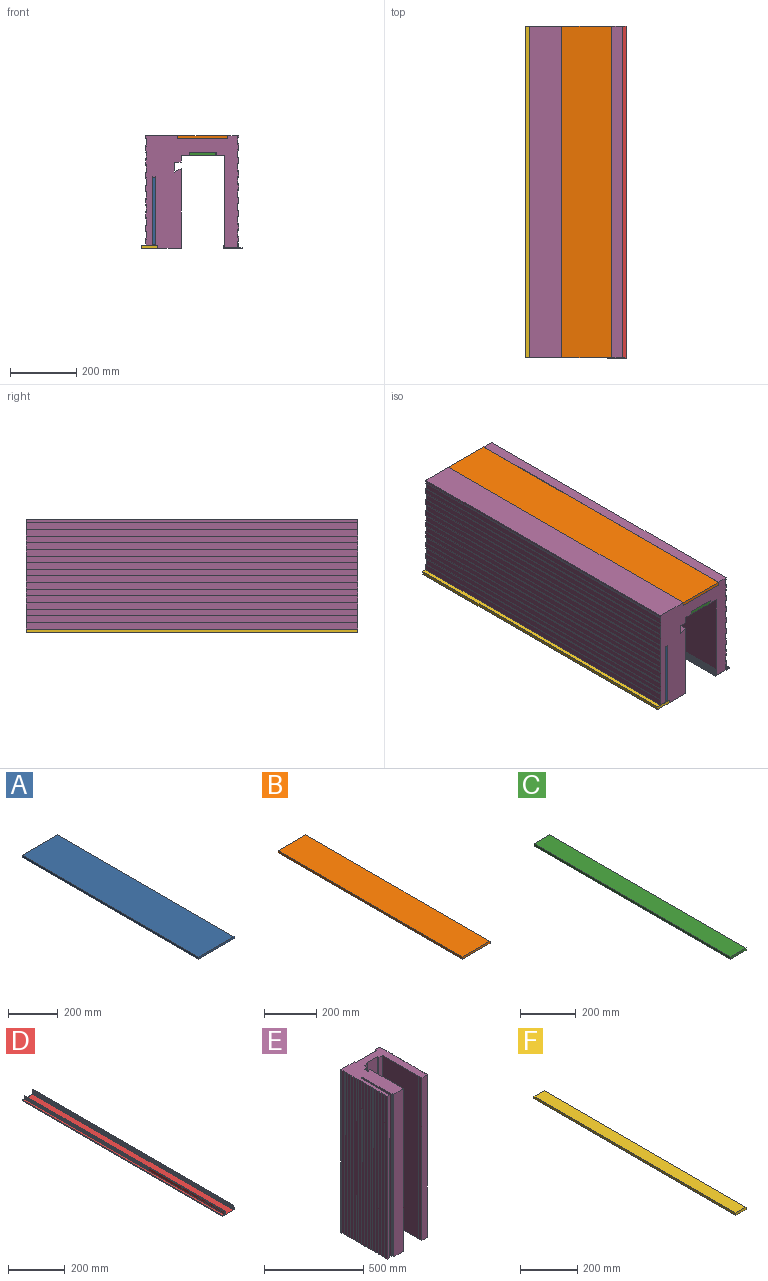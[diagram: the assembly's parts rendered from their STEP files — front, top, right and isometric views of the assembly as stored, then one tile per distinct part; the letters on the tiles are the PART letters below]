
ASSEMBLY  parts=6 mates=5
PART A: 6 faces, bbox 200x1000x10 mm
  f0: plane 1000x10mm, normal (-1,0,0), area 10000mm2, adj f1,f3,f4,f5
  f1: plane 1000x200mm, normal (0,0,-1), area 200000mm2, adj f0,f2,f4,f5
  f2: plane 1000x10mm, normal (1,0,0), area 10000mm2, adj f1,f3,f4,f5
  f3: plane 1000x200mm, normal (0,0,1), area 200000mm2, adj f0,f2,f4,f5
  f4: plane 200x10mm, normal (0,-1,0), area 2000mm2, adj f0,f1,f2,f3
  f5: plane 200x10mm, normal (0,1,0), area 2000mm2, adj f0,f1,f2,f3
PART B: 6 faces, bbox 150x1000x10 mm
  f0: plane 1000x10mm, normal (-1,0,0), area 10000mm2, adj f1,f3,f4,f5
  f1: plane 1000x150mm, normal (0,0,-1), area 150000mm2, adj f0,f2,f4,f5
  f2: plane 1000x10mm, normal (1,0,0), area 10000mm2, adj f1,f3,f4,f5
  f3: plane 1000x150mm, normal (0,0,1), area 150000mm2, adj f0,f2,f4,f5
  f4: plane 150x10mm, normal (0,-1,0), area 1500mm2, adj f0,f1,f2,f3
  f5: plane 150x10mm, normal (0,1,0), area 1500mm2, adj f0,f1,f2,f3
PART C: 6 faces, bbox 80x1000x10 mm
  f0: plane 1000x10mm, normal (-1,0,0), area 10000mm2, adj f1,f3,f4,f5
  f1: plane 1000x80mm, normal (0,0,-1), area 80000mm2, adj f0,f2,f4,f5
  f2: plane 1000x10mm, normal (1,0,0), area 10000mm2, adj f1,f3,f4,f5
  f3: plane 1000x80mm, normal (0,0,1), area 80000mm2, adj f0,f2,f4,f5
  f4: plane 80x10mm, normal (0,-1,0), area 800mm2, adj f0,f1,f2,f3
  f5: plane 80x10mm, normal (0,1,0), area 800mm2, adj f0,f1,f2,f3
PART D: 62 faces, bbox 57.5x1000x21 mm
  f0: plane 1000x14.3mm, normal (-1,0,0), area 14303.9mm2, adj f1,f2,f60,f61
  f1: plane 57.5x21mm, normal (0,-1,0), area 145.8mm2, adj f0,f2,f3,f4,f5,f6,f7,f8
  f2: plane 1000x11mm, normal (0,0,1), area 11000mm2, adj f0,f1,f3,f60
  f3: plane 1000x1.5mm, normal (1,0,0), area 1500mm2, adj f1,f2,f4,f60
  f4: plane 1000x1.5mm, normal (0,0,1), area 1500mm2, adj f1,f3,f5,f60
  f5: plane 1000x3mm, normal (-1,0,0), area 3000mm2, adj f1,f4,f6,f60
  f6: plane 1000x57.5mm, normal (0,0,-1), area 57500mm2, adj f1,f5,f7,f60
  f7: plane 1000x4mm, normal (1,0,0), area 4000mm2, adj f1,f6,f8,f60
  f8: plane 1000x1mm, normal (0,0,1), area 1000mm2, adj f1,f7,f9,f60
  f9: plane 1000x3mm, normal (-1,0,0), area 3000mm2, adj f1,f8,f10,f60
  f10: plane 1000x1mm, normal (0,0,1), area 1000mm2, adj f1,f9,f11,f60
  f11: plane 1000x7mm, normal (1,0,0), area 7000mm2, adj f1,f10,f12,f60
  f12: plane 1000x1mm, normal (0,0,-1), area 1000mm2, adj f1,f11,f13,f60
  f13: plane 1000x3mm, normal (-1,0,0), area 3000mm2, adj f1,f12,f14,f60
  f14: plane 1000x1mm, normal (0,0,-1), area 1000mm2, adj f1,f13,f15,f60
  f15: plane 1000x4mm, normal (1,0,0), area 4000mm2, adj f1,f14,f16,f60
  f16: plane 1000x2mm, normal (0,0,1), area 2000mm2, adj f1,f15,f17,f60
  f17: plane 1000x12mm, normal (1,0,0), area 12000mm2, adj f1,f16,f18,f60
  f18: plane 1000x1mm, normal (0,0,1), area 1000mm2, adj f1,f17,f19,f60
  f19: plane 1000x1.73mm, normal (-0.87,0,0.5), area 2000mm2, adj f1,f18,f20,f60
  f20: plane 1000x1mm, normal (0,0,-1), area 1000mm2, adj f1,f19,f21,f60
  f21: plane 1000x1.73mm, normal (-0.87,0,0.5), area 2000mm2, adj f1,f20,f22,f60
  f22: plane 1000x1mm, normal (0,0,-1), area 1000mm2, adj f1,f21,f23,f60
  f23: plane 1000x1.73mm, normal (-0.87,0,0.5), area 2000mm2, adj f1,f22,f24,f60
  f24: plane 1000x1mm, normal (0,0,-1), area 1000mm2, adj f1,f23,f25,f60
  f25: plane 1000x1.73mm, normal (-0.87,0,0.5), area 2000mm2, adj f1,f24,f26,f60
  f26: plane 1000x1mm, normal (0,0,-1), area 1000mm2, adj f1,f25,f27,f60
  f27: plane 1000x1.73mm, normal (-0.87,0,0.5), area 2000mm2, adj f1,f26,f28,f60
  f28: plane 1000x1mm, normal (0,0,-1), area 1000mm2, adj f1,f27,f29,f60
  f29: plane 1000x1.73mm, normal (-0.87,0,0.5), area 2000mm2, adj f1,f28,f30,f60
  f30: plane 1000x1mm, normal (0,0,-1), area 1000mm2, adj f1,f29,f31,f60
  f31: plane 1000x1.73mm, normal (-0.87,0,0.5), area 2000mm2, adj f1,f30,f32,f60
  f32: plane 1000x1mm, normal (0,0,-1), area 1000mm2, adj f1,f31,f33,f60
  f33: plane 1000x1.73mm, normal (-0.87,0,0.5), area 2000mm2, adj f1,f32,f34,f60
  f34: plane 1000x1mm, normal (0,0,-1), area 1000mm2, adj f1,f33,f35,f60
  f35: plane 1000x1.73mm, normal (-0.87,0,0.5), area 2000mm2, adj f1,f34,f36,f60
  f36: plane 1000x1mm, normal (0,0,-1), area 1000mm2, adj f1,f35,f37,f60
  f37: plane 1000x1.73mm, normal (-0.87,0,0.5), area 2000mm2, adj f1,f36,f38,f60
  f38: plane 1000x1mm, normal (0,0,-1), area 1000mm2, adj f1,f37,f39,f60
  f39: plane 1000x1.73mm, normal (-0.87,0,0.5), area 2000mm2, adj f1,f38,f40,f60
  f40: plane 1000x1mm, normal (0,0,-1), area 1000mm2, adj f1,f39,f41,f60
  f41: plane 1000x0.45mm, normal (-1,0,0), area 447.4mm2, adj f1,f40,f42,f60
  f42: plane 1000x41mm, normal (0,0,1), area 41000mm2, adj f1,f41,f43,f60
  f43: plane 1000x0.45mm, normal (1,0,0), area 447.4mm2, adj f1,f42,f44,f60
  f44: plane 1000x1mm, normal (0,0,-1), area 1000mm2, adj f1,f43,f45,f60
  f45: plane 1000x1.73mm, normal (0.87,0,0.5), area 2000mm2, adj f1,f44,f46,f60
  f46: plane 1000x1mm, normal (0,0,-1), area 1000mm2, adj f1,f45,f47,f60
  f47: plane 1000x1.73mm, normal (0.87,0,0.5), area 2000mm2, adj f1,f46,f48,f60
  f48: plane 1000x1mm, normal (0,0,-1), area 1000mm2, adj f1,f47,f49,f60
  f49: plane 1000x1.73mm, normal (0.87,0,0.5), area 2000mm2, adj f1,f48,f50,f60
  f50: plane 1000x1mm, normal (0,0,-1), area 1000mm2, adj f1,f49,f51,f60
  f51: plane 1000x1.73mm, normal (0.87,0,0.5), area 2000mm2, adj f1,f50,f52,f60
  f52: plane 1000x1mm, normal (0,0,-1), area 1000mm2, adj f1,f51,f53,f60
  f53: plane 1000x1.73mm, normal (0.87,0,0.5), area 2000mm2, adj f1,f52,f54,f60
  f54: plane 1000x1mm, normal (0,0,-1), area 1000mm2, adj f1,f53,f55,f60
  f55: plane 1000x1.73mm, normal (0.87,0,0.5), area 2000mm2, adj f1,f54,f56,f60
  f56: plane 1000x1mm, normal (0,0,-1), area 1000mm2, adj f1,f55,f57,f60
  f57: plane 1000x1.73mm, normal (0.87,0,0.5), area 2000mm2, adj f1,f56,f58,f60
  f58: plane 1000x1mm, normal (0,0,-1), area 1000mm2, adj f1,f57,f59,f60
  f59: plane 1000x1.73mm, normal (0.87,0,0.5), area 2000mm2, adj f1,f58,f60,f61
  f60: plane 57.5x21mm, normal (0,1,0), area 145.8mm2, adj f0,f2,f3,f4,f5,f6,f7,f8
  f61: plane 1000x1mm, normal (0,0,1), area 1000mm2, adj f0,f1,f59,f60
PART E: 96 faces, bbox 280x340x1000 mm
  f0: plane 1000x20mm, normal (-1,0,0), area 20000mm2, adj f46,f47,f90,f94
  f1: plane 1000x20mm, normal (-1,0,0), area 20000mm2, adj f46,f47,f87,f91
  f2: plane 1000x20mm, normal (-1,0,0), area 20000mm2, adj f46,f47,f84,f88
  f3: plane 1000x20mm, normal (-1,0,0), area 20000mm2, adj f46,f47,f81,f85
  f4: plane 1000x20mm, normal (-1,0,0), area 20000mm2, adj f46,f47,f78,f82
  f5: plane 1000x20mm, normal (-1,0,0), area 20000mm2, adj f46,f47,f75,f79
  f6: plane 1000x20mm, normal (-1,0,0), area 20000mm2, adj f46,f47,f72,f76
  f7: plane 1000x10mm, normal (-1,0,0), area 10000mm2, adj f17,f46,f47,f73
  f8: plane 1000x15mm, normal (1,0,0), area 15000mm2, adj f41,f46,f47,f69
  f9: plane 1000x20mm, normal (1,0,0), area 20000mm2, adj f46,f47,f66,f70
  f10: plane 1000x20mm, normal (1,0,0), area 20000mm2, adj f46,f47,f63,f67
  f11: plane 1000x20mm, normal (1,0,0), area 20000mm2, adj f46,f47,f60,f64
  f12: plane 1000x20mm, normal (1,0,0), area 20000mm2, adj f46,f47,f57,f61
  f13: plane 1000x20mm, normal (1,0,0), area 20000mm2, adj f46,f47,f54,f58
  f14: plane 1000x20mm, normal (1,0,0), area 20000mm2, adj f46,f47,f51,f55
  f15: plane 1000x20mm, normal (1,0,0), area 20000mm2, adj f46,f47,f48,f52
  f16: plane 1000x10mm, normal (1,0,0), area 10000mm2, adj f17,f45,f46,f47
  f17: plane 1000x96.75mm, normal (0,1,0), area 96750mm2, adj f7,f16,f46,f47
  f18: plane 1000x20mm, normal (-1,0,0), area 20000mm2, adj f19,f46,f47,f93
  f19: plane 1000x20.5mm, normal (0,-1,0), area 20500mm2, adj f18,f20,f46,f47
  f20: plane 1000x205mm, normal (1,0,0), area 205000mm2, adj f19,f21,f46,f47
  f21: cylinder r=10mm len=1000mm, axis (0,0,-1), area 11054.3mm2, adj f20,f22,f46,f47
  f22: plane 1000x205mm, normal (-1,0,0), area 205000mm2, adj f21,f23,f46,f47
  f23: plane 1000x6mm, normal (0,-1,0), area 6000mm2, adj f22,f24,f46,f47
  f24: plane 1000x10mm, normal (-1,0,0), area 10000mm2, adj f23,f25,f46,f47
  f25: plane 1000x70mm, normal (0,-1,0), area 70000mm2, adj f24,f26,f46,f47
  f26: plane 1000x240.19mm, normal (1,0,0), area 240190.5mm2, adj f25,f27,f46,f47
  f27: plane 1000x20mm, normal (-0.45,0.89,0), area 22446.5mm2, adj f26,f28,f46,f47
  f28: plane 1000x30mm, normal (1,0,0), area 30000mm2, adj f27,f29,f46,f47
  f29: plane 1000x20mm, normal (0,-1,0), area 20000mm2, adj f28,f30,f46,f47
  f30: plane 1000x20mm, normal (1,0,0), area 20000mm2, adj f29,f31,f46,f47
  f31: plane 1000x24.75mm, normal (0,-1,0), area 24750mm2, adj f30,f32,f46,f47
  f32: plane 1000x10mm, normal (1,0,0), area 10000mm2, adj f31,f33,f46,f47
  f33: plane 1000x80.5mm, normal (0,-1,0), area 80500mm2, adj f32,f34,f46,f47
  f34: plane 1000x10mm, normal (-1,0,0), area 10000mm2, adj f33,f35,f46,f47
  f35: plane 1000x24.75mm, normal (0,-1,0), area 24750mm2, adj f34,f36,f46,f47
  f36: plane 1000x257.5mm, normal (-1,0,0), area 257500mm2, adj f35,f37,f46,f47
  f37: plane 1000x2mm, normal (0,-1,0), area 2000mm2, adj f36,f38,f46,f47
  f38: plane 1000x21.5mm, normal (-1,0,0), area 21500mm2, adj f37,f39,f46,f47
  f39: plane 1000x39.1mm, normal (0,-1,0), area 39100mm2, adj f38,f40,f46,f47
  f40: plane 1000x18.5mm, normal (1,0,0), area 18500mm2, adj f39,f41,f46,f47
  f41: plane 1000x1.9mm, normal (0,-1,0), area 1900mm2, adj f8,f40,f46,f47
  f42: plane 1000x5.5mm, normal (1,0,0), area 5500mm2, adj f43,f46,f47,f49
  f43: plane 1000x32.75mm, normal (0,1,0), area 32750mm2, adj f42,f44,f46,f47
  f44: plane 1000x10mm, normal (-1,0,0), area 10000mm2, adj f43,f45,f46,f47
  f45: plane 1000x150.5mm, normal (0,1,0), area 150500mm2, adj f16,f44,f46,f47
  f46: plane 340x280mm, normal (0,0,1), area 52654.8mm2, adj f0,f1,f2,f3,f4,f5,f6,f7
  f47: plane 340x280mm, normal (0,0,-1), area 52654.8mm2, adj f0,f1,f2,f3,f4,f5,f6,f7
  f48: plane 1000x2mm, normal (-0.71,0.71,0), area 2828.4mm2, adj f15,f46,f47,f50
  f49: plane 1000x2mm, normal (-0.71,-0.71,0), area 2828.4mm2, adj f42,f46,f47,f50
  f50: plane 1000x24mm, normal (1,0,0), area 24000mm2, adj f46,f47,f48,f49
  f51: plane 1000x2mm, normal (-0.71,0.71,0), area 2828.4mm2, adj f14,f46,f47,f53
  f52: plane 1000x2mm, normal (-0.71,-0.71,0), area 2828.4mm2, adj f15,f46,f47,f53
  f53: plane 1000x24mm, normal (1,0,0), area 24000mm2, adj f46,f47,f51,f52
  f54: plane 1000x2mm, normal (-0.71,0.71,0), area 2828.4mm2, adj f13,f46,f47,f56
  f55: plane 1000x2mm, normal (-0.71,-0.71,0), area 2828.4mm2, adj f14,f46,f47,f56
  f56: plane 1000x24mm, normal (1,0,0), area 24000mm2, adj f46,f47,f54,f55
  f57: plane 1000x2mm, normal (-0.71,0.71,0), area 2828.4mm2, adj f12,f46,f47,f59
  f58: plane 1000x2mm, normal (-0.71,-0.71,0), area 2828.4mm2, adj f13,f46,f47,f59
  f59: plane 1000x24mm, normal (1,0,0), area 24000mm2, adj f46,f47,f57,f58
  f60: plane 1000x2mm, normal (-0.71,0.71,0), area 2828.4mm2, adj f11,f46,f47,f62
  f61: plane 1000x2mm, normal (-0.71,-0.71,0), area 2828.4mm2, adj f12,f46,f47,f62
  f62: plane 1000x24mm, normal (1,0,0), area 24000mm2, adj f46,f47,f60,f61
  f63: plane 1000x2mm, normal (-0.71,0.71,0), area 2828.4mm2, adj f10,f46,f47,f65
  f64: plane 1000x2mm, normal (-0.71,-0.71,0), area 2828.4mm2, adj f11,f46,f47,f65
  f65: plane 1000x24mm, normal (1,0,0), area 24000mm2, adj f46,f47,f63,f64
  f66: plane 1000x2mm, normal (-0.71,0.71,0), area 2828.4mm2, adj f9,f46,f47,f68
  f67: plane 1000x2mm, normal (-0.71,-0.71,0), area 2828.4mm2, adj f10,f46,f47,f68
  f68: plane 1000x24mm, normal (1,0,0), area 24000mm2, adj f46,f47,f66,f67
  f69: plane 1000x2mm, normal (-0.71,0.71,0), area 2828.4mm2, adj f8,f46,f47,f71
  f70: plane 1000x2mm, normal (-0.71,-0.71,0), area 2828.4mm2, adj f9,f46,f47,f71
  f71: plane 1000x24mm, normal (1,0,0), area 24000mm2, adj f46,f47,f69,f70
  f72: plane 1000x2mm, normal (0.71,0.71,0), area 2828.4mm2, adj f6,f46,f47,f74
  f73: plane 1000x2mm, normal (0.71,-0.71,0), area 2828.4mm2, adj f7,f46,f47,f74
  f74: plane 1000x24mm, normal (-1,0,0), area 24000mm2, adj f46,f47,f72,f73
  f75: plane 1000x2mm, normal (0.71,0.71,0), area 2828.4mm2, adj f5,f46,f47,f77
  f76: plane 1000x2mm, normal (0.71,-0.71,0), area 2828.4mm2, adj f6,f46,f47,f77
  f77: plane 1000x24mm, normal (-1,0,0), area 24000mm2, adj f46,f47,f75,f76
  f78: plane 1000x2mm, normal (0.71,0.71,0), area 2828.4mm2, adj f4,f46,f47,f80
  f79: plane 1000x2mm, normal (0.71,-0.71,0), area 2828.4mm2, adj f5,f46,f47,f80
  f80: plane 1000x24mm, normal (-1,0,0), area 24000mm2, adj f46,f47,f78,f79
  f81: plane 1000x2mm, normal (0.71,0.71,0), area 2828.4mm2, adj f3,f46,f47,f83
  f82: plane 1000x2mm, normal (0.71,-0.71,0), area 2828.4mm2, adj f4,f46,f47,f83
  f83: plane 1000x24mm, normal (-1,0,0), area 24000mm2, adj f46,f47,f81,f82
  f84: plane 1000x2mm, normal (0.71,0.71,0), area 2828.4mm2, adj f2,f46,f47,f86
  f85: plane 1000x2mm, normal (0.71,-0.71,0), area 2828.4mm2, adj f3,f46,f47,f86
  f86: plane 1000x24mm, normal (-1,0,0), area 24000mm2, adj f46,f47,f84,f85
  f87: plane 1000x2mm, normal (0.71,0.71,0), area 2828.4mm2, adj f1,f46,f47,f89
  f88: plane 1000x2mm, normal (0.71,-0.71,0), area 2828.4mm2, adj f2,f46,f47,f89
  f89: plane 1000x24mm, normal (-1,0,0), area 24000mm2, adj f46,f47,f87,f88
  f90: plane 1000x2mm, normal (0.71,0.71,0), area 2828.4mm2, adj f0,f46,f47,f92
  f91: plane 1000x2mm, normal (0.71,-0.71,0), area 2828.4mm2, adj f1,f46,f47,f92
  f92: plane 1000x24mm, normal (-1,0,0), area 24000mm2, adj f46,f47,f90,f91
  f93: plane 1000x2mm, normal (0.71,0.71,0), area 2828.4mm2, adj f18,f46,f47,f95
  f94: plane 1000x2mm, normal (0.71,-0.71,0), area 2828.4mm2, adj f0,f46,f47,f95
  f95: plane 1000x24mm, normal (-1,0,0), area 24000mm2, adj f46,f47,f93,f94
PART F: 6 faces, bbox 50x1000x10 mm
  f0: plane 1000x10mm, normal (-1,0,0), area 10000mm2, adj f1,f3,f4,f5
  f1: plane 1000x50mm, normal (0,0,-1), area 50000mm2, adj f0,f2,f4,f5
  f2: plane 1000x10mm, normal (1,0,0), area 10000mm2, adj f1,f3,f4,f5
  f3: plane 1000x50mm, normal (0,0,1), area 50000mm2, adj f0,f2,f4,f5
  f4: plane 50x10mm, normal (0,-1,0), area 500mm2, adj f0,f1,f2,f3
  f5: plane 50x10mm, normal (0,1,0), area 500mm2, adj f0,f1,f2,f3
PLACE A rot(axis=(0,1,0),90deg) t=(-266.83,500,-61.72)mm
PLACE B t=(-190.83,500,55.28)mm fixed
PLACE C t=(-155.83,500,5.28)mm
PLACE D rot(axis=(0,0,1),180deg) t=(-52.58,-500,-275.22)mm
PLACE E rot(axis=(1,0,0),90deg) t=(-169.34,500,-104.89)mm
PLACE F t=(-300.58,500,-274.72)mm
MATE fastened A.f4 <-> E.f46  axis (0,-1,0) through (-256.58,-500,-59.72)mm
MATE fastened E.f46 <-> B.f4  axis (0,-1,0) through (-190.83,-500,65.28)mm
MATE fastened C.f4 <-> E.f46  axis (0,-1,0) through (-155.83,-500,15.28)mm
MATE fastened D.f60 <-> E.f46  axis (0,-1,0) through (-48.58,-500,-273.72)mm
MATE fastened F.f4 <-> E.f46  axis (0,-1,0) through (-250.58,-500,-264.72)mm
